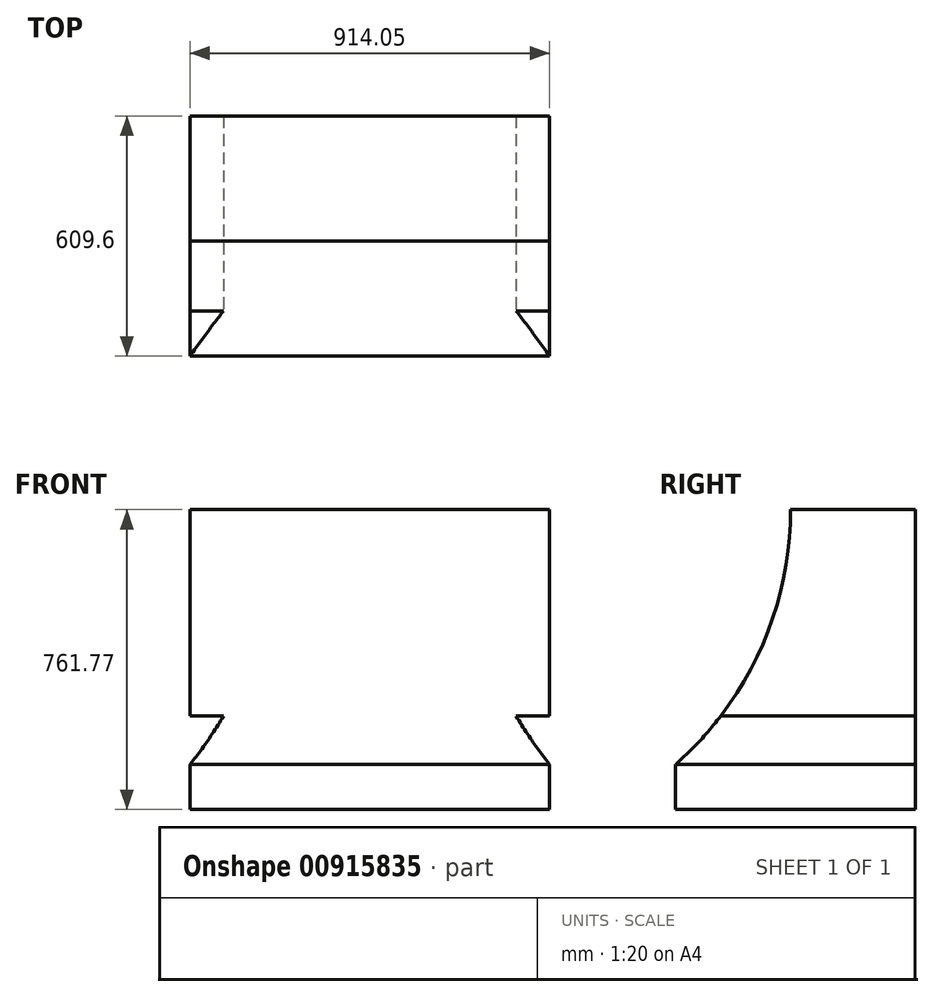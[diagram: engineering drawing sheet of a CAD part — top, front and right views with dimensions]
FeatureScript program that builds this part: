
annotation { "Feature Type Name" : "Feature", "Feature Type Description" : "" }
export const myFeature = defineFeature(function(context is Context, id is Id, definition is map)
    precondition{}
    {
        {
            var Q0;
            Q0=qCreatedBy(makeId("Front.planeOp"),FACE);
            var sketch = newSketch(context, id + "F0", { "sketchPlane" : qUnion([Q0])});
            skLineSegment(sketch, "E0.bottom", {"start": v(-457.55, 504.47) * mm, "end": v(456.85, 504.47) * mm});
            skLineSegment(sketch, "E0.top", {"start": v(-457.55, -257.53) * mm, "end": v(456.85, -257.53) * mm});
            skLineSegment(sketch, "E0.left", {"start": v(-457.55, 504.47) * mm, "end": v(-457.55, -257.53) * mm});
            skLineSegment(sketch, "E0.right", {"start": v(456.85, 504.47) * mm, "end": v(456.85, -257.53) * mm});
            skSolve(sketch);
        }
        {
            var Q0;
            Q0=makeQuery(id+"F0.imprint","IMPRINT",FACE,{"disambiguationData":[TD([[makeQuery(id+"F0.imprint","IMPRINT",EDGE,{"derivedFrom":sQuery(id+"F0.wireOp",EDGE,"E0.bottom")}),-1.0]])]});
            extrude(context, id + "F1", {"entities" : qUnion([Q0]), "depth" : 609.6 * mm, "offsetDistance" : 25.4 * mm});
        }
        {
            var Q0;
            Q0=makeQuery(id+"F1.opExtrude","SWEPT_BODY",BODY,{"disambiguationData":[OSD([sQuery(id+"F0.wireOp",EDGE,"E0.bottom"),sQuery(id+"F0.wireOp",EDGE,"E0.top"),sQuery(id+"F0.wireOp",EDGE,"E0.left"),sQuery(id+"F0.wireOp",EDGE,"E0.right")])]});
            transform(context, id + "F2", {"entities" : qUnion([Q0]), "transformType" : TransformType.TRANSLATION_3D, "dx" : 1143 * mm, "dy" : 0 * mm, "dz" : 0 * mm, "makeCopy" : false});
        }
        {
            var Q0;
            Q0=qCreatedBy(makeId("Front.planeOp"),FACE);
            var sketch = newSketch(context, id + "F3", { "sketchPlane" : qUnion([Q0])});
            skLineSegment(sketch, "E1.bottom", {"start": v(-457.2, 381) * mm, "end": v(457.2, 381) * mm});
            skLineSegment(sketch, "E1.top", {"start": v(-457.2, -381) * mm, "end": v(457.2, -381) * mm});
            skLineSegment(sketch, "E1.left", {"start": v(-457.2, 381) * mm, "end": v(-457.2, -381) * mm});
            skLineSegment(sketch, "E1.right", {"start": v(457.2, 381) * mm, "end": v(457.2, -381) * mm});
            skPoint(sketch, "E1.middle", {"position": v(0, 0) * mm});
            skSolve(sketch);
        }
        {
            var Q0;
            Q0=makeQuery(id+"F3.imprint","IMPRINT",FACE,{"disambiguationData":[TD([[makeQuery(id+"F3.imprint","IMPRINT",EDGE,{"derivedFrom":sQuery(id+"F3.wireOp",EDGE,"E1.bottom")}),-1.0]])]});
            extrude(context, id + "F4", {"entities" : qUnion([Q0]), "depth" : 609.6 * mm, "offsetDistance" : 25.4 * mm});
        }
        {
            var Q0;
            Q0=makeQuery(id+"F1.opExtrude","SWEPT_FACE",FACE,{"disambiguationData":[OSD([sQuery(id+"F0.wireOp",EDGE,"E0.right")])]});
            var sketch = newSketch(context, id + "F5", { "sketchPlane" : qUnion([Q0])});
            skArc(sketch, "E2", {"start": v(-609.6, -143.23) * mm, "mid": v(-393.9, 149.21) * mm, "end": v(-317.5, 504.47) * mm});
            skSolve(sketch);
        }
        {
            var Q0;
            {var subQ0=sQuery(id+"F5.wireOp",EDGE,"E2");Q0=makeQuery(id+"F5.imprint","IMPRINT",FACE,{"disambiguationData":[TD([[makeQuery(id+"F5.imprint","IMPRINT",EDGE,{"derivedFrom":subQ0}),1.0]])]});}
            extrude(context, id + "F6", {"entities" : qUnion([Q0]), "operationType" : NewBodyOperationType.REMOVE, "endBound" : BoundingType.THROUGH_ALL, "oppositeDirection" : true, "depth" : 25.4 * mm, "offsetDistance" : 25.4 * mm});
        }
        {
            var Q0;
            Q0=makeQuery(id+"F4.opExtrude","CAP_FACE",FACE,{"disambiguationData":[OSD([sQuery(id+"F3.wireOp",EDGE,"E1.bottom"),sQuery(id+"F3.wireOp",EDGE,"E1.top"),sQuery(id+"F3.wireOp",EDGE,"E1.left"),sQuery(id+"F3.wireOp",EDGE,"E1.right")])],"isStart":false});
            var sketch = newSketch(context, id + "F7", { "sketchPlane" : qUnion([Q0])});
            skArc(sketch, "E3", {"start": v(-457.2, -266.7) * mm, "mid": v(-287.43, 37.57) * mm, "end": v(-228.6, 381) * mm});
            skArc(sketch, "E4", {"start": v(228.6, 381) * mm, "mid": v(287.43, 37.57) * mm, "end": v(457.2, -266.7) * mm});
            skSolve(sketch);
        }
        {
            var Q0;
            {var subQ0=sQuery(id+"F7.wireOp",EDGE,"E3");Q0=makeQuery(id+"F7.imprint","IMPRINT",FACE,{"disambiguationData":[TD([[makeQuery(id+"F7.imprint","IMPRINT",EDGE,{"derivedFrom":subQ0}),1.0]])]});}
            var Q1;
            {var subQ0=sQuery(id+"F7.wireOp",EDGE,"E4");Q1=makeQuery(id+"F7.imprint","IMPRINT",FACE,{"disambiguationData":[TD([[makeQuery(id+"F7.imprint","IMPRINT",EDGE,{"derivedFrom":subQ0}),1.0]])]});}
            extrude(context, id + "F8", {"entities" : qUnion([Q0, Q1]), "operationType" : NewBodyOperationType.REMOVE, "endBound" : BoundingType.THROUGH_ALL, "oppositeDirection" : true, "depth" : 25.4 * mm, "offsetDistance" : 25.4 * mm});
        }
        {
            var Q0;
            Q0=makeQuery(id+"F1.opExtrude","SWEPT_BODY",BODY,{"disambiguationData":[OSD([sQuery(id+"F0.wireOp",EDGE,"E0.bottom"),sQuery(id+"F0.wireOp",EDGE,"E0.top"),sQuery(id+"F0.wireOp",EDGE,"E0.left"),sQuery(id+"F0.wireOp",EDGE,"E0.right")])]});
            transform(context, id + "F9", {"entities" : qUnion([Q0]), "transformType" : TransformType.TRANSLATION_3D, "dx" : -1143 * mm, "dy" : 0 * mm, "dz" : -123.24 * mm, "makeCopy" : false});
        }
        {
            var Q0;
            Q0=makeQuery(id+"F1.opExtrude","SWEPT_BODY",BODY,{"disambiguationData":[OSD([sQuery(id+"F0.wireOp",EDGE,"E0.bottom"),sQuery(id+"F0.wireOp",EDGE,"E0.top"),sQuery(id+"F0.wireOp",EDGE,"E0.left"),sQuery(id+"F0.wireOp",EDGE,"E0.right")])]});
            var Q1;
            Q1=makeQuery(id+"F4.opExtrude","SWEPT_BODY",BODY,{"disambiguationData":[OSD([sQuery(id+"F3.wireOp",EDGE,"E1.bottom"),sQuery(id+"F3.wireOp",EDGE,"E1.top"),sQuery(id+"F3.wireOp",EDGE,"E1.left"),sQuery(id+"F3.wireOp",EDGE,"E1.right")])]});
            booleanBodies(context, id + "F10", {"operationType" : BooleanOperationType.INTERSECTION, "tools" : qUnion([Q0, Q1])});
        }
    });
